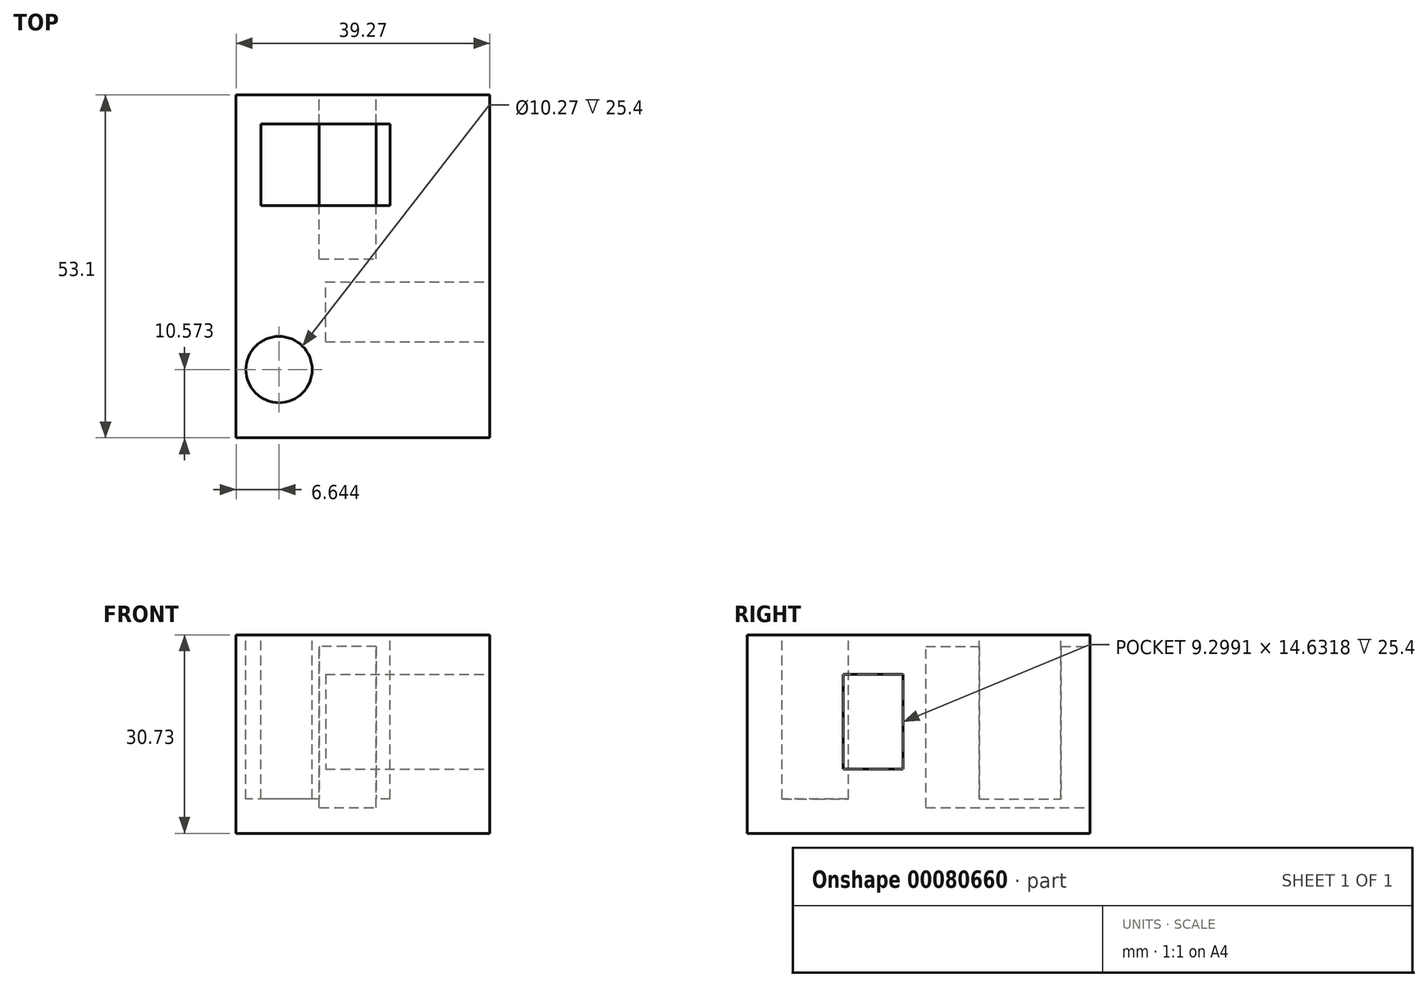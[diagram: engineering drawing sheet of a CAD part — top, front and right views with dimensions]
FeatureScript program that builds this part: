
annotation { "Feature Type Name" : "Feature", "Feature Type Description" : "" }
export const myFeature = defineFeature(function(context is Context, id is Id, definition is map)
    precondition{}
    {
        {
            var Q0;
            Q0=qCreatedBy(makeId("Top.planeOp"),FACE);
            var sketch = newSketch(context, id + "F0", { "sketchPlane" : qUnion([Q0])});
            skLineSegment(sketch, "E0.bottom", {"start": v(-28.85, 21.48) * mm, "end": v(10.42, 21.48) * mm});
            skLineSegment(sketch, "E0.top", {"start": v(-28.85, -31.62) * mm, "end": v(10.42, -31.62) * mm});
            skLineSegment(sketch, "E0.left", {"start": v(-28.85, 21.48) * mm, "end": v(-28.85, -31.62) * mm});
            skLineSegment(sketch, "E0.right", {"start": v(10.42, 21.48) * mm, "end": v(10.42, -31.62) * mm});
            skSolve(sketch);
        }
        {
            var Q0;
            Q0 = qSketchRegion(id + "F0", true);
            extrude(context, id + "F1", {"entities" : qUnion([Q0]), "depth" : 30.73 * mm, "offsetDistance" : 25.4 * mm});
        }
        {
            var Q0;
            Q0=makeQuery(id+"F1.opExtrude","SWEPT_FACE",FACE,{"disambiguationData":[OSD([sQuery(id+"F0.wireOp",EDGE,"E0.bottom")])]});
            var sketch = newSketch(context, id + "F2", { "sketchPlane" : qUnion([Q0])});
            skCircle(sketch, "E1", {"center": v(0, 21.76) * mm, "radius": 5.9 * mm});
            skSolve(sketch);
        }
        {
            var Q0;
            Q0=makeQuery(id+"F2.imprint","IMPRINT",FACE,{"disambiguationData":[TD([[makeQuery(id+"F2.imprint","IMPRINT",EDGE,{"derivedFrom":sQuery(id+"F2.wireOp",EDGE,"E1")}),1.0]])]});
            extrude(context, id + "F3", {"entities" : qUnion([Q0]), "operationType" : NewBodyOperationType.ADD, "oppositeDirection" : true, "depth" : 34.54 * mm, "offsetDistance" : 25.4 * mm});
        }
        {
            var Q0;
            Q0=makeQuery(id+"F1.opExtrude","SWEPT_FACE",FACE,{"disambiguationData":[OSD([sQuery(id+"F0.wireOp",EDGE,"E0.bottom")])]});
            var sketch = newSketch(context, id + "F4", { "sketchPlane" : qUnion([Q0])});
            skCircle(sketch, "E2", {"center": v(0, 17.77) * mm, "radius": 6.94 * mm});
            skSolve(sketch);
        }
        {
            var Q0;
            Q0 = qSketchRegion(id + "F4", true);
            extrude(context, id + "F5", {"entities" : qUnion([Q0]), "operationType" : NewBodyOperationType.ADD, "oppositeDirection" : true, "depth" : 29.2 * mm, "offsetDistance" : 25.4 * mm});
        }
        {
            var Q0;
            Q0=makeQuery(id+"F1.opExtrude","CAP_FACE",FACE,{"disambiguationData":[OSD([sQuery(id+"F0.wireOp",EDGE,"E0.bottom"),sQuery(id+"F0.wireOp",EDGE,"E0.top"),sQuery(id+"F0.wireOp",EDGE,"E0.left"),sQuery(id+"F0.wireOp",EDGE,"E0.right")])],"isStart":false});
            var sketch = newSketch(context, id + "F6", { "sketchPlane" : qUnion([Q0])});
            skCircle(sketch, "E3", {"center": v(-22.2, -21.05) * mm, "radius": 5.14 * mm});
            skSolve(sketch);
        }
        {
            var Q0;
            Q0 = qSketchRegion(id + "F6", true);
            extrude(context, id + "F7", {"entities" : qUnion([Q0]), "operationType" : NewBodyOperationType.REMOVE, "oppositeDirection" : true, "depth" : 25.4 * mm, "offsetDistance" : 25.4 * mm});
        }
        {
            var Q0;
            Q0=makeQuery(id+"F1.opExtrude","SWEPT_FACE",FACE,{"disambiguationData":[OSD([sQuery(id+"F0.wireOp",EDGE,"E0.right")])]});
            var sketch = newSketch(context, id + "F8", { "sketchPlane" : qUnion([Q0])});
            skLineSegment(sketch, "E4.bottom", {"start": v(-16.76, 24.6) * mm, "end": v(-7.46, 24.6) * mm});
            skLineSegment(sketch, "E4.top", {"start": v(-16.76, 9.96) * mm, "end": v(-7.46, 9.96) * mm});
            skLineSegment(sketch, "E4.left", {"start": v(-16.76, 24.6) * mm, "end": v(-16.76, 9.96) * mm});
            skLineSegment(sketch, "E4.right", {"start": v(-7.46, 24.6) * mm, "end": v(-7.46, 9.96) * mm});
            skSolve(sketch);
        }
        {
            var Q0;
            Q0 = qSketchRegion(id + "F8", true);
            extrude(context, id + "F9", {"entities" : qUnion([Q0]), "operationType" : NewBodyOperationType.REMOVE, "oppositeDirection" : true, "depth" : 25.4 * mm, "offsetDistance" : 25.4 * mm});
        }
        {
            var Q0;
            Q0=makeQuery(id+"F1.opExtrude","SWEPT_FACE",FACE,{"disambiguationData":[OSD([sQuery(id+"F0.wireOp",EDGE,"E0.bottom")])]});
            var sketch = newSketch(context, id + "F10", { "sketchPlane" : qUnion([Q0])});
            skLineSegment(sketch, "E5.bottom", {"start": v(15.97, 4) * mm, "end": v(7.15, 4) * mm});
            skLineSegment(sketch, "E5.top", {"start": v(15.97, 28.92) * mm, "end": v(7.15, 28.92) * mm});
            skLineSegment(sketch, "E5.left", {"start": v(15.97, 4) * mm, "end": v(15.97, 28.92) * mm});
            skLineSegment(sketch, "E5.right", {"start": v(7.15, 4) * mm, "end": v(7.15, 28.92) * mm});
            skSolve(sketch);
        }
        {
            var Q0;
            Q0 = qSketchRegion(id + "F10", true);
            extrude(context, id + "F11", {"entities" : qUnion([Q0]), "operationType" : NewBodyOperationType.REMOVE, "oppositeDirection" : true, "depth" : 25.4 * mm, "offsetDistance" : 25.4 * mm});
        }
        {
            var Q0;
            Q0=makeQuery(id+"F1.opExtrude","CAP_FACE",FACE,{"disambiguationData":[OSD([sQuery(id+"F0.wireOp",EDGE,"E0.bottom"),sQuery(id+"F0.wireOp",EDGE,"E0.top"),sQuery(id+"F0.wireOp",EDGE,"E0.left"),sQuery(id+"F0.wireOp",EDGE,"E0.right")])],"isStart":false});
            var sketch = newSketch(context, id + "F12", { "sketchPlane" : qUnion([Q0])});
            skLineSegment(sketch, "E6.bottom", {"start": v(-5, 4.36) * mm, "end": v(-25, 4.36) * mm});
            skLineSegment(sketch, "E6.top", {"start": v(-5, 17) * mm, "end": v(-25, 17) * mm});
            skLineSegment(sketch, "E6.left", {"start": v(-5, 4.36) * mm, "end": v(-5, 17) * mm});
            skLineSegment(sketch, "E6.right", {"start": v(-25, 4.36) * mm, "end": v(-25, 17) * mm});
            skSolve(sketch);
        }
        {
            var Q0;
            Q0 = qSketchRegion(id + "F12", true);
            extrude(context, id + "F13", {"entities" : qUnion([Q0]), "operationType" : NewBodyOperationType.REMOVE, "oppositeDirection" : true, "depth" : 25.4 * mm, "offsetDistance" : 25.4 * mm});
        }
    });
